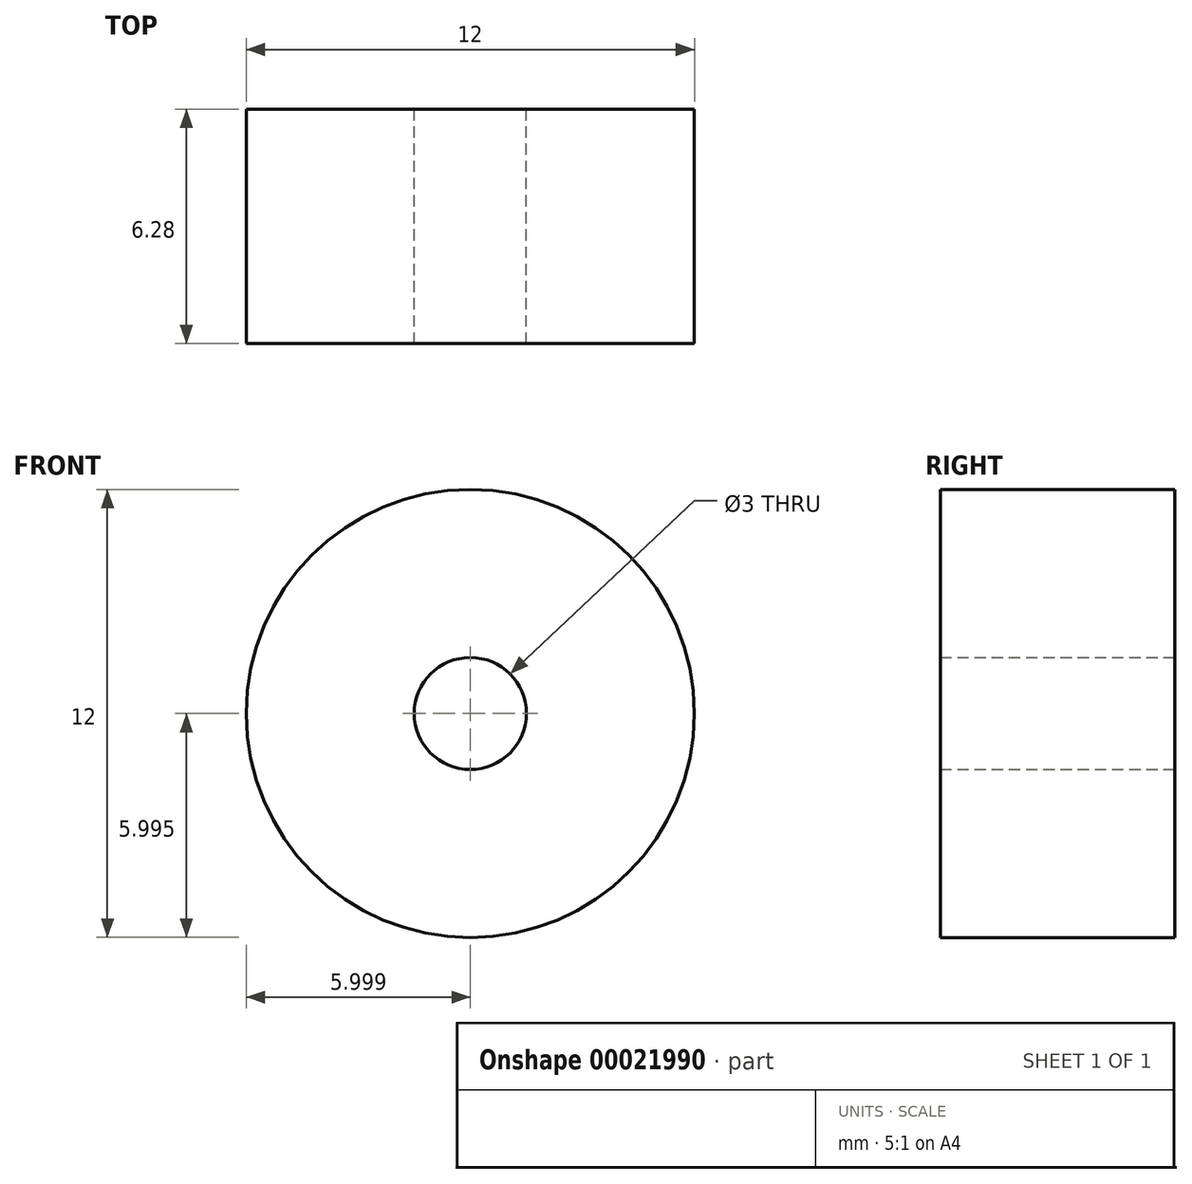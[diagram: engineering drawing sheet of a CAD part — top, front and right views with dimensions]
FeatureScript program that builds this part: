
annotation { "Feature Type Name" : "Feature", "Feature Type Description" : "" }
export const myFeature = defineFeature(function(context is Context, id is Id, definition is map)
    precondition{}
    {
        {
            var Q0;
            Q0=qCreatedBy(makeId("Front.planeOp"),FACE);
            var sketch = newSketch(context, id + "F0", { "sketchPlane" : qUnion([Q0])});
            skCircle(sketch, "E0", {"center": v(-0.8, 1.2) * mm, "radius": 6 * mm});
            skCircle(sketch, "E1", {"center": v(-0.8, 1.2) * mm, "radius": 1.5 * mm});
            skSolve(sketch);
        }
        {
            var Q0;
            Q0=makeQuery(id+"F0.imprint","IMPRINT",FACE,{"disambiguationData":[TD([[makeQuery(id+"F0.imprint","IMPRINT",EDGE,{"derivedFrom":sQuery(id+"F0.wireOp",EDGE,"E0")}),1.0]])]});
            extrude(context, id + "F1", {"entities" : qUnion([Q0]), "endBound" : BoundingType.SYMMETRIC, "depth" : 6.28 * mm});
        }
    });
